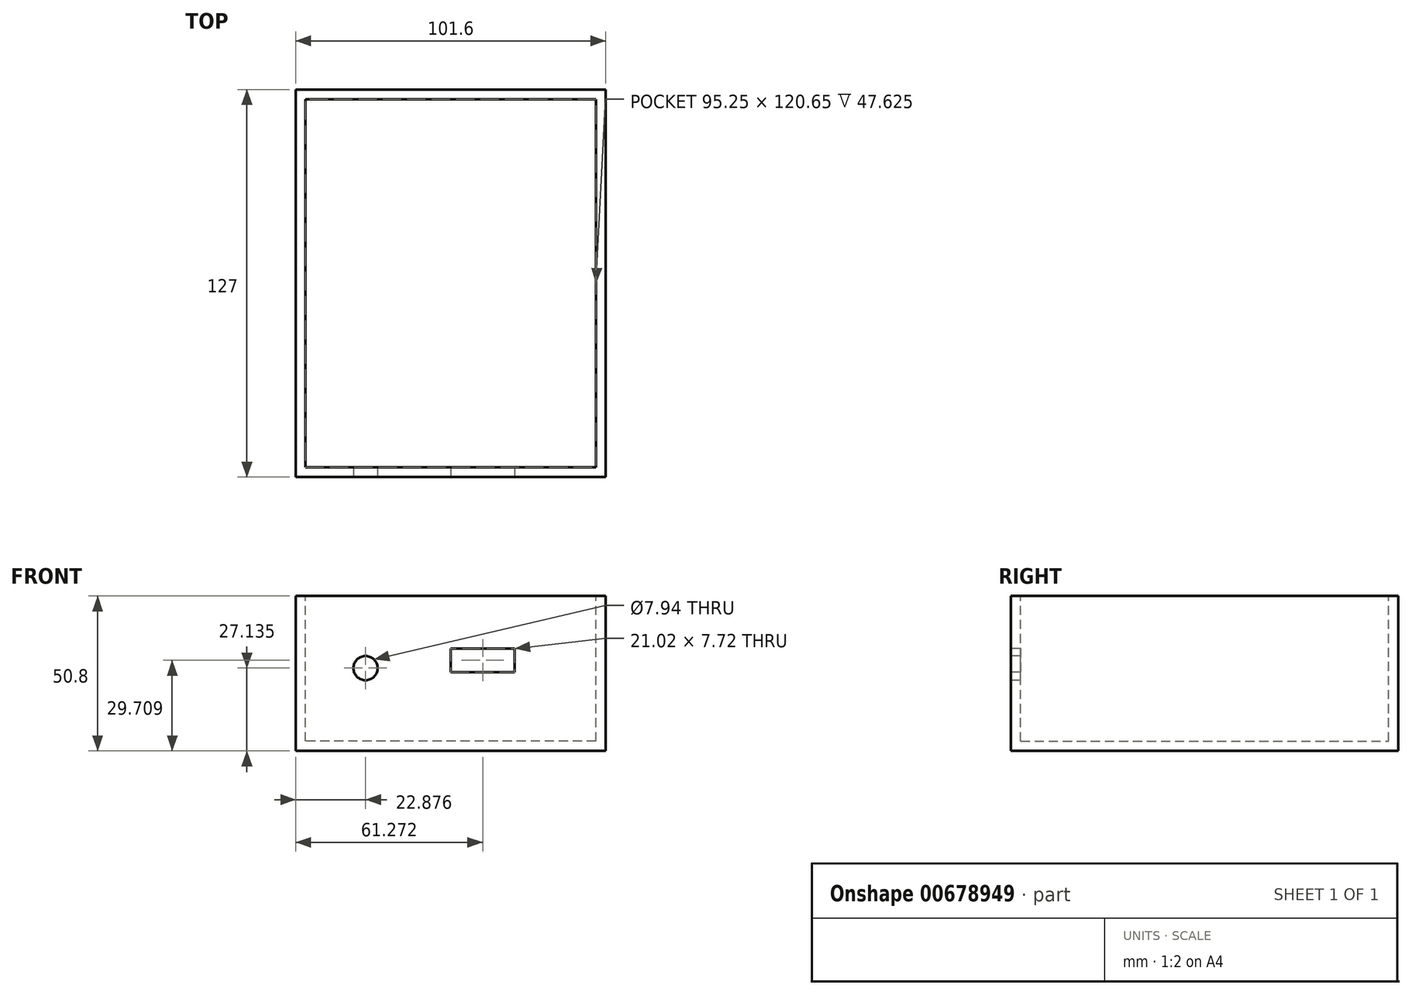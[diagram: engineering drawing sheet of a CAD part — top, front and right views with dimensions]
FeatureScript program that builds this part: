
annotation { "Feature Type Name" : "Feature", "Feature Type Description" : "" }
export const myFeature = defineFeature(function(context is Context, id is Id, definition is map)
    precondition{}
    {
        {
            var Q0;
            Q0=qCreatedBy(makeId("Front.planeOp"),FACE);
            var sketch = newSketch(context, id + "F0", { "sketchPlane" : qUnion([Q0])});
            skLineSegment(sketch, "E0.bottom", {"start": v(16, 0) * mm, "end": v(-85.6, 0) * mm});
            skLineSegment(sketch, "E0.top", {"start": v(16, 50.8) * mm, "end": v(-85.6, 50.8) * mm});
            skLineSegment(sketch, "E0.left", {"start": v(16, 0) * mm, "end": v(16, 50.8) * mm});
            skLineSegment(sketch, "E0.right", {"start": v(-85.6, 0) * mm, "end": v(-85.6, 50.8) * mm});
            skPoint(sketch, "E0.middle", {"position": v(-34.8, 25.4) * mm});
            skSolve(sketch);
        }
        {
            var Q0;
            Q0=makeQuery(id+"F0.imprint","IMPRINT",FACE,{"disambiguationData":[TD([[makeQuery(id+"F0.imprint","IMPRINT",EDGE,{"derivedFrom":sQuery(id+"F0.wireOp",EDGE,"E0.bottom")}),-1.0]])]});
            extrude(context, id + "F1", {"entities" : qUnion([Q0]), "depth" : 127 * mm, "offsetDistance" : 25.4 * mm});
        }
        {
            var Q0;
            Q0=makeQuery(id+"F1.opExtrude","SWEPT_FACE",FACE,{"disambiguationData":[OSD([sQuery(id+"F0.wireOp",EDGE,"E0.top")])]});
            shell(context, id + "F2", {"entities" : qUnion([Q0]), "thickness" : 3.17 * mm});
        }
        {
            var Q0;
            Q0=makeQuery(id+"F1.opExtrude","CAP_FACE",FACE,{"disambiguationData":[OSD([sQuery(id+"F0.wireOp",EDGE,"E0.bottom"),sQuery(id+"F0.wireOp",EDGE,"E0.top"),sQuery(id+"F0.wireOp",EDGE,"E0.left"),sQuery(id+"F0.wireOp",EDGE,"E0.right")])],"isStart":false});
            var sketch = newSketch(context, id + "F3", { "sketchPlane" : qUnion([Q0])});
            skPoint(sketch, "E1", {"position": v(-62.72, 27.13) * mm});
            skSolve(sketch);
        }
        {
            var Q0;
            Q0=sQuery(id+"F3.wireOp",VERTEX,"E1");
            var Q1;
            Q1=makeQuery(id+"F1.opExtrude","SWEPT_BODY",BODY,{"disambiguationData":[OSD([sQuery(id+"F0.wireOp",EDGE,"E0.bottom"),sQuery(id+"F0.wireOp",EDGE,"E0.top"),sQuery(id+"F0.wireOp",EDGE,"E0.left"),sQuery(id+"F0.wireOp",EDGE,"E0.right")])]});
            hole(context, id + "F4", {"style" : HoleStyle.SIMPLE, "endStyle" : HoleEndStyle.BLIND, "holeDiameter" : 7.94 * mm, "majorDiameter" : 6.35 * mm, "holeDepth" : 12.7 * mm, "isTappedThrough" : true, "tappedDepth" : 12.7 * mm, "tapClearance" : 3, "locations" : qUnion([Q0]), "scope" : qUnion([Q1])});
        }
        {
            var Q0;
            Q0=makeQuery(id+"F1.opExtrude","CAP_FACE",FACE,{"disambiguationData":[OSD([sQuery(id+"F0.wireOp",EDGE,"E0.bottom"),sQuery(id+"F0.wireOp",EDGE,"E0.top"),sQuery(id+"F0.wireOp",EDGE,"E0.left"),sQuery(id+"F0.wireOp",EDGE,"E0.right")])],"isStart":false});
            var sketch = newSketch(context, id + "F5", { "sketchPlane" : qUnion([Q0])});
            skLineSegment(sketch, "E2.bottom", {"start": v(-13.82, 25.85) * mm, "end": v(-34.84, 25.85) * mm});
            skLineSegment(sketch, "E2.top", {"start": v(-13.82, 33.57) * mm, "end": v(-34.84, 33.57) * mm});
            skLineSegment(sketch, "E2.left", {"start": v(-13.82, 25.85) * mm, "end": v(-13.82, 33.57) * mm});
            skLineSegment(sketch, "E2.right", {"start": v(-34.84, 25.85) * mm, "end": v(-34.84, 33.57) * mm});
            skPoint(sketch, "E2.middle", {"position": v(-24.33, 29.7) * mm});
            skSolve(sketch);
        }
        {
            var Q0;
            Q0=makeQuery(id+"F5.imprint","IMPRINT",FACE,{"disambiguationData":[TD([[makeQuery(id+"F5.imprint","IMPRINT",EDGE,{"derivedFrom":sQuery(id+"F5.wireOp",EDGE,"E2.bottom")}),-1.0]])]});
            extrude(context, id + "F6", {"entities" : qUnion([Q0]), "operationType" : NewBodyOperationType.REMOVE, "endBound" : BoundingType.UP_TO_NEXT, "oppositeDirection" : true, "depth" : 25.4 * mm, "offsetDistance" : 25.4 * mm});
        }
    });
